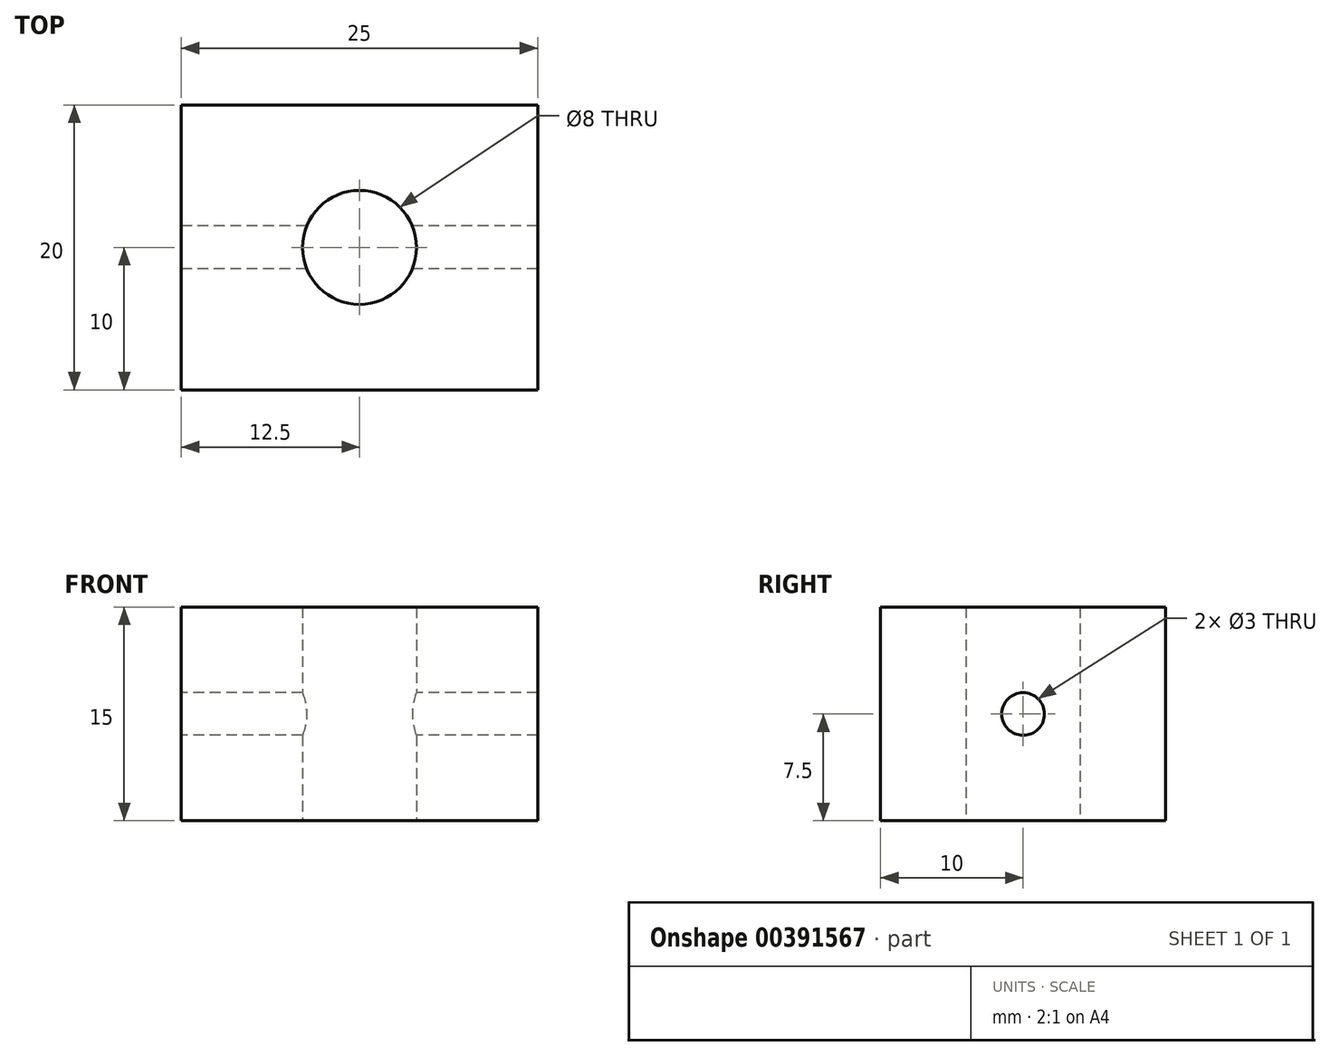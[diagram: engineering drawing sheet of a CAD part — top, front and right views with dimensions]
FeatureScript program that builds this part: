
annotation { "Feature Type Name" : "Feature", "Feature Type Description" : "" }
export const myFeature = defineFeature(function(context is Context, id is Id, definition is map)
    precondition{}
    {
        {
            var Q0;
            Q0=qCreatedBy(makeId("Top.planeOp"),FACE);
            var sketch = newSketch(context, id + "F0", { "sketchPlane" : qUnion([Q0])});
            skLineSegment(sketch, "E0.bottom", {"start": v(0, 0) * mm, "end": v(-25, 0) * mm});
            skLineSegment(sketch, "E0.top", {"start": v(0, 20) * mm, "end": v(-25, 20) * mm});
            skLineSegment(sketch, "E0.left", {"start": v(0, 0) * mm, "end": v(0, 20) * mm});
            skLineSegment(sketch, "E0.right", {"start": v(-25, 0) * mm, "end": v(-25, 20) * mm});
            skLineSegment(sketch, "E1", {"start": v(-25, 20) * mm, "end": v(-12.5, 20) * mm});
            skLineSegment(sketch, "E2", {"start": v(-12.5, 20) * mm, "end": v(-12.5, 0) * mm, "construction": true});
            skPoint(sketch, "E3.orphan", {"position": v(-25, 10) * mm});
            skPoint(sketch, "E4.end.orphan", {"position": v(0, 10) * mm});
            skCircle(sketch, "E5", {"center": v(-12.5, 10) * mm, "radius": 4 * mm});
            skSolve(sketch);
        }
        {
            var Q0;
            Q0=makeQuery(id+"F0.imprint","IMPRINT",FACE,{"disambiguationData":[TD([[makeQuery(id+"F0.imprint","IMPRINT",EDGE,{"derivedFrom":sQuery(id+"F0.wireOp",EDGE,"E0.bottom")}),-1.0]])]});
            extrude(context, id + "F1", {"entities" : qUnion([Q0]), "depth" : 15 * mm});
        }
        {
            var Q0;
            Q0=makeQuery(id+"F1.opExtrude","SWEPT_FACE",FACE,{"disambiguationData":[OSD([sQuery(id+"F0.wireOp",EDGE,"E0.right")])]});
            var sketch = newSketch(context, id + "F2", { "sketchPlane" : qUnion([Q0])});
            skLineSegment(sketch, "E6", {"start": v(-20, 7.5) * mm, "end": v(0, 7.5) * mm, "construction": true});
            skCircle(sketch, "E7", {"center": v(-10, 7.5) * mm, "radius": 1.5 * mm});
            skSolve(sketch);
        }
        {
            var Q0;
            Q0=makeQuery(id+"F2.imprint","IMPRINT",FACE,{"disambiguationData":[TD([[makeQuery(id+"F2.imprint","IMPRINT",EDGE,{"derivedFrom":sQuery(id+"F2.wireOp",EDGE,"E7")}),1.0]])]});
            extrude(context, id + "F3", {"entities" : qUnion([Q0]), "operationType" : NewBodyOperationType.REMOVE, "oppositeDirection" : true, "depth" : 50 * mm});
        }
    });
